# Revit family: QF_MACOM_EASYCOOK
name_source: partatom
category: Equipamento especial
units: mm (PartAtom-declared; Revit-internal decimal feet)

## family parameters
Com base no plano de trabalho = Não
Compartilhado = Não
Corte com vazios quando carregada = Não
Cota do conector redondo = Utilizar diâmetro
Número OmniClass = 23.40.40.14.17.11
Ponto de cálculo do ambiente = Não
Sempre na vertical = Sim
Tipo de parte = Normal
Título OmniClass = Cookers, Ovens, Stoves

## types (1)
- EASYCOOK
    Capacity in Liters = 10,5 L
    Cycle = 60 Hz
    Degree of Protection = IP 23
    Depth = 754 mm
    Descrição = EASYCOOK ELÉTRICO MACOM
    Elec Connection Height = 169 mm
    Electric Power = 8000 W
    Electrical Supply = 220 V
    Elevação padrão = 0 mm
    Fabricante = MACOM
    Height = 993 mm
    Modelo = EASYCOOK
    Operational Current = 36 A
    Show Clearances = Sim
    URL = https://www.acosmacom.com.br
    Volume = 0,43 m³
    Weight = 70,00 kg
    Width = 583 mm
    Work Temperature = 80 ºC - 185 ºC
